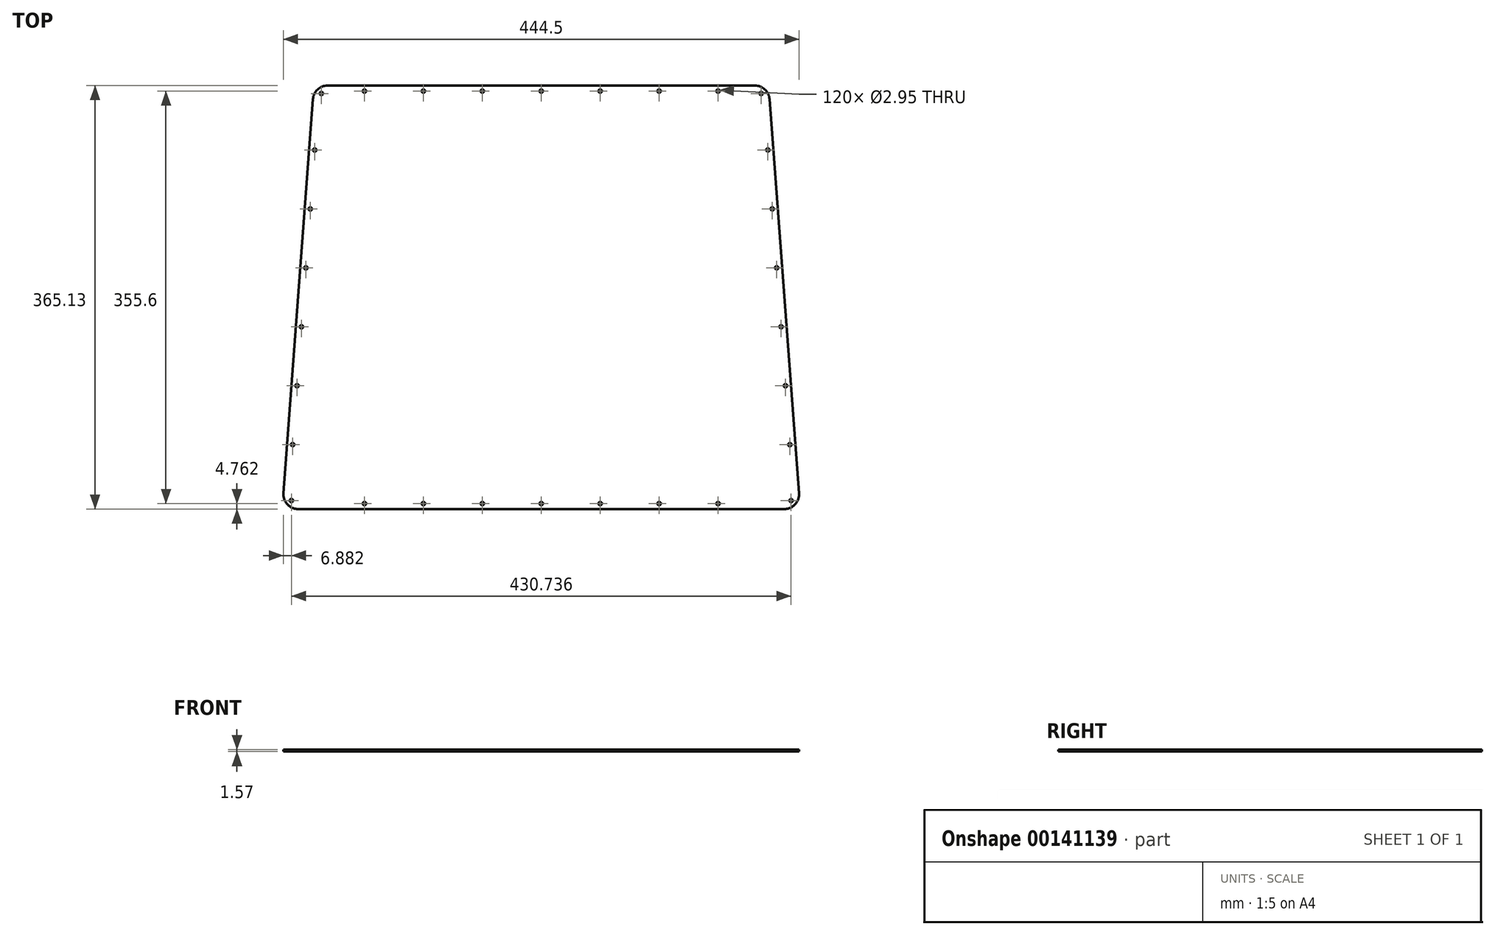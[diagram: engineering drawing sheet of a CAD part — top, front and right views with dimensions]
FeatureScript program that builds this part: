
annotation { "Feature Type Name" : "Feature", "Feature Type Description" : "" }
export const myFeature = defineFeature(function(context is Context, id is Id, definition is map)
    precondition{}
    {
        {
            var Q0;
            Q0=qCreatedBy(makeId("Top.planeOp"),FACE);
            var sketch = newSketch(context, id + "F0", { "sketchPlane" : qUnion([Q0])});
            skLineSegment(sketch, "E0", {"start": v(-209.55, 0) * mm, "end": v(-53.97, 0) * mm, "construction": true});
            skLineSegment(sketch, "E1", {"start": v(209.55, 0) * mm, "end": v(184.15, 339.73) * mm, "construction": true});
            skLineSegment(sketch, "E2", {"start": v(184.15, 339.73) * mm, "end": v(53.97, 339.73) * mm, "construction": true});
            skLineSegment(sketch, "E3", {"start": v(-184.15, 339.73) * mm, "end": v(-209.55, 0) * mm, "construction": true});
            skLineSegment(sketch, "E4", {"start": v(0, 0) * mm, "end": v(0, 339.73) * mm, "construction": true});
            skLineSegment(sketch, "E5", {"start": v(-53.98, 339.73) * mm, "end": v(-53.98, 0) * mm, "construction": true});
            skLineSegment(sketch, "E6", {"start": v(53.97, 339.73) * mm, "end": v(53.97, 0) * mm, "construction": true});
            skLineSegment(sketch, "E7.trimOffspring", {"start": v(-53.98, 339.73) * mm, "end": v(-184.15, 339.73) * mm, "construction": true});
            skLineSegment(sketch, "E8.trimOffspring", {"start": v(53.97, 0) * mm, "end": v(209.55, 0) * mm, "construction": true});
            skLineSegment(sketch, "E9", {"start": v(-53.97, 0) * mm, "end": v(53.97, 0) * mm, "construction": true});
            skLineSegment(sketch, "E10.0", {"start": v(-53.98, 352.43) * mm, "end": v(-184.15, 352.43) * mm});
            skLineSegment(sketch, "E10.1", {"start": v(-41.28, 339.73) * mm, "end": v(-41.27, 0) * mm, "construction": true});
            skLineSegment(sketch, "E10.2", {"start": v(-209.55, -12.7) * mm, "end": v(-53.97, -12.7) * mm});
            skLineSegment(sketch, "E10.3", {"start": v(-196.81, 340.67) * mm, "end": v(-222.21, 0.95) * mm});
            skLineSegment(sketch, "E11.0", {"start": v(184.15, 352.43) * mm, "end": v(53.97, 352.43) * mm});
            skLineSegment(sketch, "E11.1", {"start": v(222.21, 0.95) * mm, "end": v(196.81, 340.67) * mm});
            skLineSegment(sketch, "E11.2", {"start": v(53.98, -12.7) * mm, "end": v(209.55, -12.7) * mm});
            skLineSegment(sketch, "E11.3", {"start": v(41.27, 339.73) * mm, "end": v(41.27, 0) * mm, "construction": true});
            skPoint(sketch, "E12.visualSharp", {"position": v(-41.28, 352.43) * mm});
            skArc(sketch, "E12.filletArc", {"start": v(-41.28, 339.73) * mm, "mid": v(-45, 348.7) * mm, "end": v(-53.98, 352.43) * mm, "construction": true});
            skPoint(sketch, "E13.visualSharp", {"position": v(-195.94, 352.43) * mm});
            skArc(sketch, "E13.filletArc", {"start": v(-184.15, 352.43) * mm, "mid": v(-192.79, 349.03) * mm, "end": v(-196.81, 340.67) * mm});
            skPoint(sketch, "E14.visualSharp", {"position": v(-223.23, -12.7) * mm});
            skArc(sketch, "E14.filletArc", {"start": v(-222.21, 0.95) * mm, "mid": v(-218.86, -8.64) * mm, "end": v(-209.55, -12.7) * mm});
            skPoint(sketch, "E15.visualSharp", {"position": v(-41.27, -12.7) * mm});
            skArc(sketch, "E15.filletArc", {"start": v(-53.97, -12.7) * mm, "mid": v(-45, -8.98) * mm, "end": v(-41.27, 0) * mm, "construction": true});
            skPoint(sketch, "E16.visualSharp", {"position": v(41.27, -12.7) * mm});
            skArc(sketch, "E16.filletArc", {"start": v(41.28, 0) * mm, "mid": v(45, -8.98) * mm, "end": v(53.98, -12.7) * mm, "construction": true});
            skPoint(sketch, "E17.visualSharp", {"position": v(223.23, -12.7) * mm});
            skArc(sketch, "E17.filletArc", {"start": v(209.55, -12.7) * mm, "mid": v(218.86, -8.64) * mm, "end": v(222.21, 0.95) * mm});
            skPoint(sketch, "E18.visualSharp", {"position": v(195.94, 352.43) * mm});
            skArc(sketch, "E18.filletArc", {"start": v(196.81, 340.67) * mm, "mid": v(192.79, 349.03) * mm, "end": v(184.15, 352.43) * mm});
            skPoint(sketch, "E19.visualSharp", {"position": v(41.27, 352.43) * mm});
            skArc(sketch, "E19.filletArc", {"start": v(53.97, 352.43) * mm, "mid": v(45, 348.7) * mm, "end": v(41.27, 339.73) * mm, "construction": true});
            skLineSegment(sketch, "E20", {"start": v(-53.98, 352.43) * mm, "end": v(53.97, 352.43) * mm});
            skLineSegment(sketch, "E21", {"start": v(-53.97, -12.7) * mm, "end": v(53.98, -12.7) * mm});
            skSolve(sketch);
        }
        {
            var Q0;
            Q0=makeQuery(id+"F0.imprint","IMPRINT",FACE,{"disambiguationData":[TD([[makeQuery(id+"F0.imprint","IMPRINT",EDGE,{"derivedFrom":sQuery(id+"F0.wireOp",EDGE,"E10.0")}),1.0]])]});
            extrude(context, id + "F1", {"entities" : qUnion([Q0]), "depth" : 1.57 * mm});
        }
        {
            var Q0;
            Q0=makeQuery(id+"F1.opExtrude","CAP_FACE",FACE,{"disambiguationData":[OSD([sQuery(id+"F0.wireOp",EDGE,"E10.0"),sQuery(id+"F0.wireOp",EDGE,"E10.1"),sQuery(id+"F0.wireOp",EDGE,"E10.2"),sQuery(id+"F0.wireOp",EDGE,"E10.3"),sQuery(id+"F0.wireOp",EDGE,"E12.filletArc"),sQuery(id+"F0.wireOp",EDGE,"E13.filletArc"),sQuery(id+"F0.wireOp",EDGE,"E14.filletArc"),sQuery(id+"F0.wireOp",EDGE,"E15.filletArc")])],"isStart":false});
            var sketch = newSketch(context, id + "F2", { "sketchPlane" : qUnion([Q0])});
            skLineSegment(sketch, "E22.1", {"start": v(-192.07, 340.32) * mm, "end": v(-217.47, 0.6) * mm});
            skLineSegment(sketch, "E22.2", {"start": v(-184.15, 347.66) * mm, "end": v(184.15, 347.66) * mm});
            skLineSegment(sketch, "E22.5", {"start": v(217.47, 0.6) * mm, "end": v(192.07, 340.32) * mm});
            skLineSegment(sketch, "E22.7", {"start": v(-209.55, -7.94) * mm, "end": v(209.55, -7.94) * mm});
            skLineSegment(sketch, "E23", {"start": v(-195.31, 296.86) * mm, "end": v(195.31, 296.86) * mm});
            skLineSegment(sketch, "E24", {"start": v(199.11, 246.06) * mm, "end": v(-199.11, 246.06) * mm});
            skLineSegment(sketch, "E25", {"start": v(202.91, 195.26) * mm, "end": v(-202.91, 195.26) * mm});
            skLineSegment(sketch, "E26", {"start": v(206.7, 144.46) * mm, "end": v(-206.7, 144.46) * mm});
            skLineSegment(sketch, "E27", {"start": v(210.5, 93.66) * mm, "end": v(-210.5, 93.66) * mm});
            skLineSegment(sketch, "E28", {"start": v(214.3, 42.86) * mm, "end": v(-214.3, 42.86) * mm});
            skLineSegment(sketch, "E29", {"start": v(-77.4, 347.66) * mm, "end": v(-77.4, 296.86) * mm});
            skLineSegment(sketch, "E30", {"start": v(-77.4, 296.86) * mm, "end": v(-77.4, 246.06) * mm});
            skLineSegment(sketch, "E31", {"start": v(-77.4, 246.06) * mm, "end": v(-77.4, 195.26) * mm});
            skLineSegment(sketch, "E32", {"start": v(-77.4, 195.26) * mm, "end": v(-77.4, 144.46) * mm});
            skLineSegment(sketch, "E33", {"start": v(-77.4, 144.46) * mm, "end": v(-77.4, 93.66) * mm});
            skLineSegment(sketch, "E34", {"start": v(-77.4, 93.66) * mm, "end": v(-77.4, 42.86) * mm});
            skPoint(sketch, "E35", {"position": v(-195.31, 296.86) * mm});
            skPoint(sketch, "E36", {"position": v(-199.11, 246.06) * mm});
            skPoint(sketch, "E37", {"position": v(-202.91, 195.26) * mm});
            skPoint(sketch, "E38", {"position": v(-206.7, 144.46) * mm});
            skPoint(sketch, "E39", {"position": v(-210.5, 93.66) * mm});
            skPoint(sketch, "E40", {"position": v(-214.3, 42.86) * mm});
            skPoint(sketch, "E41", {"position": v(214.3, 42.86) * mm});
            skPoint(sketch, "E42", {"position": v(210.5, 93.66) * mm});
            skPoint(sketch, "E43", {"position": v(206.7, 144.46) * mm});
            skPoint(sketch, "E44", {"position": v(202.91, 195.26) * mm});
            skPoint(sketch, "E45", {"position": v(199.11, 246.06) * mm});
            skPoint(sketch, "E46", {"position": v(195.31, 296.86) * mm});
            skLineSegment(sketch, "E47", {"start": v(-152.4, 347.66) * mm, "end": v(-152.4, -7.94) * mm});
            skLineSegment(sketch, "E48", {"start": v(-50.8, -7.94) * mm, "end": v(-50.8, 347.66) * mm});
            skLineSegment(sketch, "E49", {"start": v(-101.6, 347.66) * mm, "end": v(-101.6, -7.94) * mm});
            skLineSegment(sketch, "E50", {"start": v(0, 347.66) * mm, "end": v(0, -7.94) * mm});
            skLineSegment(sketch, "E51", {"start": v(50.8, 347.66) * mm, "end": v(50.8, -7.94) * mm});
            skLineSegment(sketch, "E52", {"start": v(101.6, 347.66) * mm, "end": v(101.6, -7.94) * mm});
            skLineSegment(sketch, "E53", {"start": v(-152.4, 12.17) * mm, "end": v(-101.6, 12.17) * mm});
            skLineSegment(sketch, "E54", {"start": v(-101.6, 12.17) * mm, "end": v(-50.8, 12.17) * mm});
            skLineSegment(sketch, "E55", {"start": v(-50.8, 12.17) * mm, "end": v(0, 12.17) * mm});
            skLineSegment(sketch, "E56", {"start": v(0, 12.17) * mm, "end": v(50.8, 12.17) * mm});
            skLineSegment(sketch, "E57", {"start": v(50.8, 12.17) * mm, "end": v(101.6, 12.17) * mm});
            skLineSegment(sketch, "E58", {"start": v(152.4, 347.66) * mm, "end": v(152.4, -7.94) * mm});
            skLineSegment(sketch, "E59", {"start": v(101.6, 12.17) * mm, "end": v(152.4, 12.17) * mm});
            skPoint(sketch, "E60", {"position": v(-152.4, 347.66) * mm});
            skPoint(sketch, "E61", {"position": v(-101.6, 347.66) * mm});
            skPoint(sketch, "E62", {"position": v(-50.8, 347.66) * mm});
            skPoint(sketch, "E63", {"position": v(0, 347.66) * mm});
            skPoint(sketch, "E64", {"position": v(50.8, 347.66) * mm});
            skPoint(sketch, "E65", {"position": v(101.6, 347.66) * mm});
            skPoint(sketch, "E66", {"position": v(152.4, 347.66) * mm});
            skPoint(sketch, "E67", {"position": v(152.4, -7.94) * mm});
            skPoint(sketch, "E68", {"position": v(101.6, -7.94) * mm});
            skPoint(sketch, "E69", {"position": v(50.8, -7.94) * mm});
            skPoint(sketch, "E70", {"position": v(0, -7.94) * mm});
            skPoint(sketch, "E71", {"position": v(-50.8, -7.94) * mm});
            skPoint(sketch, "E72", {"position": v(-101.6, -7.94) * mm});
            skPoint(sketch, "E73", {"position": v(-152.4, -7.94) * mm});
            skArc(sketch, "E74", {"start": v(-192.07, 340.32) * mm, "mid": v(-189.55, 345.54) * mm, "end": v(-184.15, 347.66) * mm});
            skArc(sketch, "E75", {"start": v(-209.55, -7.94) * mm, "mid": v(-215.37, -5.4) * mm, "end": v(-217.47, 0.6) * mm});
            skArc(sketch, "E76", {"start": v(209.55, -7.94) * mm, "mid": v(215.37, -5.4) * mm, "end": v(217.47, 0.6) * mm});
            skArc(sketch, "E77", {"start": v(192.07, 340.32) * mm, "mid": v(189.55, 345.54) * mm, "end": v(184.15, 347.66) * mm});
            skPoint(sketch, "E78", {"position": v(-215.37, -5.4) * mm});
            skPoint(sketch, "E79", {"position": v(-189.55, 345.54) * mm});
            skPoint(sketch, "E80", {"position": v(189.55, 345.54) * mm});
            skPoint(sketch, "E81", {"position": v(215.37, -5.4) * mm});
            skSolve(sketch);
        }
        {
            var Q0;
            Q0=sQuery(id+"F2.wireOp",VERTEX,"48fa61f3-92d6-45ac-9f99-2f0877b615d5");
            var Q1;
            Q1=sQuery(id+"F2.wireOp",VERTEX,"E60");
            var Q2;
            Q2=sQuery(id+"F2.wireOp",VERTEX,"E61");
            var Q3;
            Q3=sQuery(id+"F2.wireOp",VERTEX,"E62");
            var Q4;
            Q4=sQuery(id+"F2.wireOp",VERTEX,"E63");
            var Q5;
            Q5=sQuery(id+"F2.wireOp",VERTEX,"E64");
            var Q6;
            Q6=sQuery(id+"F2.wireOp",VERTEX,"E65");
            var Q7;
            Q7=sQuery(id+"F2.wireOp",VERTEX,"E66");
            var Q8;
            Q8=sQuery(id+"F2.wireOp",VERTEX,"1278468f-ea45-4261-b4bb-7df7e37ad81e");
            var Q9;
            Q9=sQuery(id+"F2.wireOp",VERTEX,"E46");
            var Q10;
            Q10=sQuery(id+"F2.wireOp",VERTEX,"E45");
            var Q11;
            Q11=sQuery(id+"F2.wireOp",VERTEX,"E44");
            var Q12;
            Q12=sQuery(id+"F2.wireOp",VERTEX,"E43");
            var Q13;
            Q13=sQuery(id+"F2.wireOp",VERTEX,"E42");
            var Q14;
            Q14=sQuery(id+"F2.wireOp",VERTEX,"E41");
            var Q15;
            Q15=sQuery(id+"F2.wireOp",VERTEX,"7be23c0f-4732-4dd1-beeb-99f7ec7cd3d6");
            var Q16;
            Q16=sQuery(id+"F2.wireOp",VERTEX,"E67");
            var Q17;
            Q17=sQuery(id+"F2.wireOp",VERTEX,"E68");
            var Q18;
            Q18=sQuery(id+"F2.wireOp",VERTEX,"E69");
            var Q19;
            Q19=sQuery(id+"F2.wireOp",VERTEX,"E70");
            var Q20;
            Q20=sQuery(id+"F2.wireOp",VERTEX,"E71");
            var Q21;
            Q21=sQuery(id+"F2.wireOp",VERTEX,"E72");
            var Q22;
            Q22=sQuery(id+"F2.wireOp",VERTEX,"E73");
            var Q23;
            Q23=sQuery(id+"F2.wireOp",VERTEX,"a7fa1f5b-f09e-4978-adeb-f64f854eb7fa");
            var Q24;
            Q24=sQuery(id+"F2.wireOp",VERTEX,"E40");
            var Q25;
            Q25=sQuery(id+"F2.wireOp",VERTEX,"E39");
            var Q26;
            Q26=sQuery(id+"F2.wireOp",VERTEX,"E38");
            var Q27;
            Q27=sQuery(id+"F2.wireOp",VERTEX,"E37");
            var Q28;
            Q28=sQuery(id+"F2.wireOp",VERTEX,"E36");
            var Q29;
            Q29=sQuery(id+"F2.wireOp",VERTEX,"E35");
            var Q30;
            Q30=sQuery(id+"F2.wireOp",VERTEX,"E81");
            var Q31;
            Q31=sQuery(id+"F2.wireOp",VERTEX,"E78");
            var Q32;
            Q32=sQuery(id+"F2.wireOp",VERTEX,"E79");
            var Q33;
            Q33=sQuery(id+"F2.wireOp",VERTEX,"E80");
            var Q34;
            Q34=makeQuery(id+"F1.opExtrude","SWEPT_BODY",BODY,{"disambiguationData":[OSD([sQuery(id+"F0.wireOp",EDGE,"E10.0"),sQuery(id+"F0.wireOp",EDGE,"E10.1"),sQuery(id+"F0.wireOp",EDGE,"E10.2"),sQuery(id+"F0.wireOp",EDGE,"E10.3"),sQuery(id+"F0.wireOp",EDGE,"E12.filletArc"),sQuery(id+"F0.wireOp",EDGE,"E13.filletArc"),sQuery(id+"F0.wireOp",EDGE,"E14.filletArc"),sQuery(id+"F0.wireOp",EDGE,"E15.filletArc")])]});
            hole(context, id + "F3", {"style" : HoleStyle.SIMPLE, "endStyle" : HoleEndStyle.THROUGH, "standardTappedOrClearance" : lookupTablePath({ "standard" : "ANSI", "fit" : "Close", "size" : "#4", "type" : "Clearance" }), "standardBlindInLast" : lookupTablePath({ "fit" : "Close", "standard" : "ANSI", "size" : "#4", "type" : "Clearance" }), "holeDiameter" : 2.95 * mm, "startFromSketch" : true, "locations" : qUnion([Q0, Q1, Q2, Q3, Q4, Q5, Q6, Q7, Q8, Q9, Q10, Q11, Q12, Q13, Q14, Q15, Q16, Q17, Q18, Q19, Q20, Q21, Q22, Q23, Q24, Q25, Q26, Q27, Q28, Q29, Q30, Q31, Q32, Q33]), "scope" : qUnion([Q34]), "isTappedThrough" : true});
        }
        {
            var Q0;
            Q0=makeQuery(id+"F1.opExtrude","SWEPT_BODY",BODY,{"disambiguationData":[OSD([sQuery(id+"F0.wireOp",EDGE,"E10.0"),sQuery(id+"F0.wireOp",EDGE,"E10.1"),sQuery(id+"F0.wireOp",EDGE,"E10.2"),sQuery(id+"F0.wireOp",EDGE,"E10.3"),sQuery(id+"F0.wireOp",EDGE,"E12.filletArc"),sQuery(id+"F0.wireOp",EDGE,"E13.filletArc"),sQuery(id+"F0.wireOp",EDGE,"E14.filletArc"),sQuery(id+"F0.wireOp",EDGE,"E15.filletArc")])]});
            var Q1;
            Q1=qCreatedBy(makeId("Right.planeOp"),FACE);
            mirror(context, id + "F4", {"entities" : qUnion([Q0]), "mirrorPlane" : qUnion([Q1])});
        }
    });
